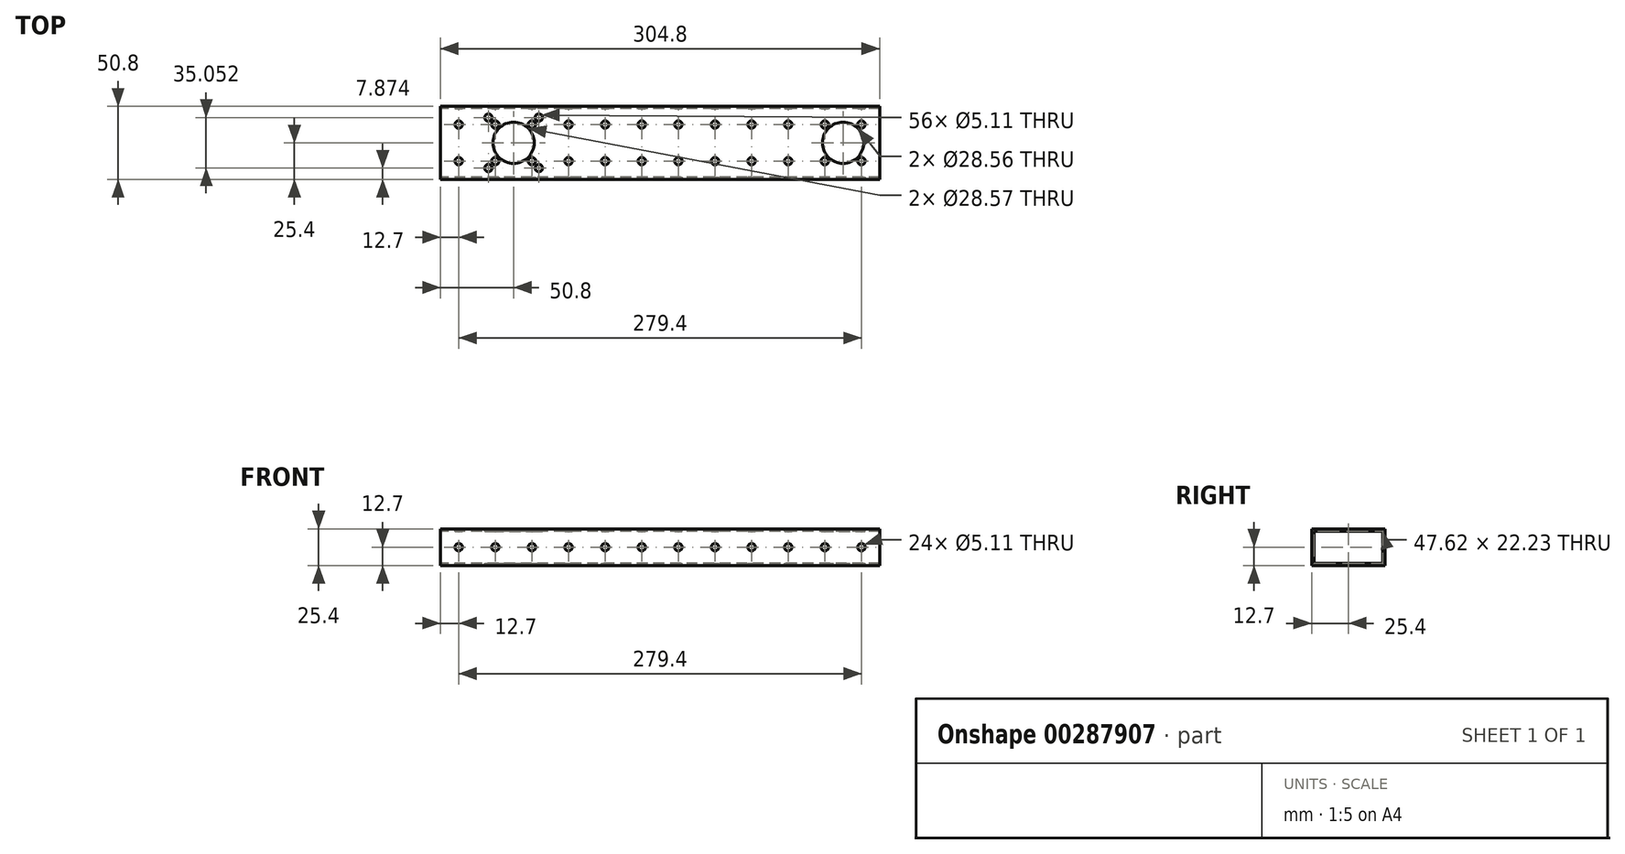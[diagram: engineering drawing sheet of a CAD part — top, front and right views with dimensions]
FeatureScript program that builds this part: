
annotation { "Feature Type Name" : "Feature", "Feature Type Description" : "" }
export const myFeature = defineFeature(function(context is Context, id is Id, definition is map)
    precondition{}
    {
        {
            var Q0;
            Q0=qCreatedBy(makeId("Right.planeOp"),FACE);
            var sketch = newSketch(context, id + "F0", { "sketchPlane" : qUnion([Q0])});
            skLineSegment(sketch, "E0.bottom", {"start": v(25.4, 12.7) * mm, "end": v(-25.4, 12.7) * mm});
            skLineSegment(sketch, "E0.top", {"start": v(25.4, -12.7) * mm, "end": v(-25.4, -12.7) * mm});
            skLineSegment(sketch, "E0.left", {"start": v(25.4, 12.7) * mm, "end": v(25.4, -12.7) * mm});
            skLineSegment(sketch, "E0.right", {"start": v(-25.4, 12.7) * mm, "end": v(-25.4, -12.7) * mm});
            skPoint(sketch, "E0.middle", {"position": v(0, 0) * mm});
            skLineSegment(sketch, "E1.bottom", {"start": v(23.81, 11.11) * mm, "end": v(-23.81, 11.11) * mm});
            skLineSegment(sketch, "E1.top", {"start": v(23.81, -11.11) * mm, "end": v(-23.81, -11.11) * mm});
            skLineSegment(sketch, "E1.left", {"start": v(23.81, 11.11) * mm, "end": v(23.81, -11.11) * mm});
            skLineSegment(sketch, "E1.right", {"start": v(-23.81, 11.11) * mm, "end": v(-23.81, -11.11) * mm});
            skSolve(sketch);
        }
        {
            var Q0;
            Q0 = qSketchRegion(id + "F0", true);
            extrude(context, id + "F1", {"entities" : qUnion([Q0]), "depth" : 304.8 * mm});
        }
        {
            var Q0;
            Q0=makeQuery(id+"F1.opExtrude","SWEPT_FACE",FACE,{"disambiguationData":[OSD([sQuery(id+"F0.wireOp",EDGE,"E0.bottom")])]});
            var sketch = newSketch(context, id + "F2", { "sketchPlane" : qUnion([Q0])});
            skCircle(sketch, "E2", {"center": v(279.4, 0) * mm, "radius": 14.28 * mm});
            skSolve(sketch);
        }
        {
            var Q0;
            Q0 = qSketchRegion(id + "F2", true);
            extrude(context, id + "F3", {"entities" : qUnion([Q0]), "operationType" : NewBodyOperationType.REMOVE, "endBound" : BoundingType.THROUGH_ALL, "oppositeDirection" : true, "depth" : 25.4 * mm});
        }
        {
            var Q0;
            Q0=makeQuery(id+"F1.opExtrude","SWEPT_FACE",FACE,{"disambiguationData":[OSD([sQuery(id+"F0.wireOp",EDGE,"E0.bottom")])]});
            var sketch = newSketch(context, id + "F4", { "sketchPlane" : qUnion([Q0])});
            skLineSegment(sketch, "E3", {"start": v(25.4, 25.4) * mm, "end": v(25.4, -25.4) * mm, "construction": true});
            skCircle(sketch, "E4", {"center": v(50.8, 0) * mm, "radius": 14.29 * mm});
            skLineSegment(sketch, "E5.bottom", {"start": v(68.33, -17.53) * mm, "end": v(33.27, -17.53) * mm, "construction": true});
            skLineSegment(sketch, "E5.top", {"start": v(68.33, 17.53) * mm, "end": v(33.27, 17.53) * mm, "construction": true});
            skLineSegment(sketch, "E5.left", {"start": v(68.33, -17.53) * mm, "end": v(68.33, 17.53) * mm, "construction": true});
            skLineSegment(sketch, "E5.right", {"start": v(33.27, -17.53) * mm, "end": v(33.27, 17.53) * mm, "construction": true});
            skCircle(sketch, "E6", {"center": v(68.33, 17.53) * mm, "radius": 2.55 * mm});
            skCircle(sketch, "E7", {"center": v(68.33, -17.53) * mm, "radius": 2.55 * mm});
            skCircle(sketch, "E8", {"center": v(33.27, -17.53) * mm, "radius": 2.55 * mm});
            skCircle(sketch, "E9", {"center": v(33.27, 17.53) * mm, "radius": 2.55 * mm});
            skPoint(sketch, "E10", {"position": v(279.4, 0) * mm});
            skSolve(sketch);
        }
        {
            var Q0;
            Q0 = qSketchRegion(id + "F4", true);
            extrude(context, id + "F5", {"entities" : qUnion([Q0]), "operationType" : NewBodyOperationType.REMOVE, "endBound" : BoundingType.THROUGH_ALL, "oppositeDirection" : true, "depth" : 25.4 * mm});
        }
        {
            var Q0;
            Q0=makeQuery(id+"F1.opExtrude","SWEPT_FACE",FACE,{"disambiguationData":[OSD([sQuery(id+"F0.wireOp",EDGE,"E0.right")])]});
            var sketch = newSketch(context, id + "F6", { "sketchPlane" : qUnion([Q0])});
            skCircle(sketch, "E11", {"center": v(12.7, 0) * mm, "radius": 2.55 * mm});
            skCircle(sketch, "E12.1.0.0", {"center": v(38.1, 0) * mm, "radius": 2.55 * mm});
            skCircle(sketch, "E12.2.0.0", {"center": v(63.5, 0) * mm, "radius": 2.55 * mm});
            skCircle(sketch, "E12.3.0.0", {"center": v(88.9, 0) * mm, "radius": 2.55 * mm});
            skCircle(sketch, "E12.4.0.0", {"center": v(114.3, 0) * mm, "radius": 2.55 * mm});
            skCircle(sketch, "E12.5.0.0", {"center": v(139.7, 0) * mm, "radius": 2.55 * mm});
            skCircle(sketch, "E12.6.0.0", {"center": v(165.1, 0) * mm, "radius": 2.55 * mm});
            skCircle(sketch, "E12.7.0.0", {"center": v(190.5, 0) * mm, "radius": 2.55 * mm});
            skCircle(sketch, "E12.8.0.0", {"center": v(215.9, 0) * mm, "radius": 2.55 * mm});
            skCircle(sketch, "E12.9.0.0", {"center": v(241.3, 0) * mm, "radius": 2.55 * mm});
            skCircle(sketch, "E12.10.0.0", {"center": v(266.7, 0) * mm, "radius": 2.55 * mm});
            skCircle(sketch, "E12.11.0.0", {"center": v(292.1, 0) * mm, "radius": 2.55 * mm});
            skLineSegment(sketch, "E12.direction1", {"start": v(12.7, 0) * mm, "end": v(38.1, 0) * mm, "construction": true});
            skSolve(sketch);
        }
        {
            var Q0;
            Q0=sQuery(id+"F6.wireOp",VERTEX,"E12.6.0.0.center");
            var Q1;
            Q1=sQuery(id+"F6.wireOp",VERTEX,"E12.5.0.0.center");
            var Q2;
            Q2=sQuery(id+"F6.wireOp",VERTEX,"E12.2.0.0.center");
            var Q3;
            Q3=sQuery(id+"F6.wireOp",VERTEX,"E12.4.0.0.center");
            var Q4;
            Q4=sQuery(id+"F6.wireOp",VERTEX,"E12.10.0.0.center");
            var Q5;
            Q5=sQuery(id+"F6.wireOp",VERTEX,"E12.3.0.0.center");
            var Q6;
            Q6=sQuery(id+"F6.wireOp",VERTEX,"E11.center");
            var Q7;
            Q7=sQuery(id+"F6.wireOp",VERTEX,"E12.7.0.0.center");
            var Q8;
            Q8=sQuery(id+"F6.wireOp",VERTEX,"E12.9.0.0.center");
            var Q9;
            Q9=sQuery(id+"F6.wireOp",VERTEX,"E12.8.0.0.center");
            var Q10;
            Q10=sQuery(id+"F6.wireOp",VERTEX,"E12.11.0.0.center");
            var Q11;
            Q11=sQuery(id+"F6.wireOp",VERTEX,"E12.direction1.end");
            var Q12;
            Q12=makeQuery(id+"F1.opExtrude","SWEPT_BODY",BODY,{"disambiguationData":[OSD([sQuery(id+"F0.wireOp",EDGE,"E0.bottom"),sQuery(id+"F0.wireOp",EDGE,"E0.top"),sQuery(id+"F0.wireOp",EDGE,"E0.left"),sQuery(id+"F0.wireOp",EDGE,"E0.right"),sQuery(id+"F0.wireOp",EDGE,"E1.bottom"),sQuery(id+"F0.wireOp",EDGE,"E1.top"),sQuery(id+"F0.wireOp",EDGE,"E1.left"),sQuery(id+"F0.wireOp",EDGE,"E1.right")])]});
            hole(context, id + "F7", {"style" : HoleStyle.SIMPLE, "endStyle" : HoleEndStyle.THROUGH, "holeDiameter" : 5.1 * mm, "tappedDepth" : 12.7 * mm, "tapClearance" : 3, "locations" : qUnion([Q0, Q1, Q2, Q3, Q4, Q5, Q6, Q7, Q8, Q9, Q10, Q11]), "scope" : qUnion([Q12])});
        }
        {
            var Q0;
            Q0=makeQuery(id+"F1.opExtrude","SWEPT_FACE",FACE,{"disambiguationData":[OSD([sQuery(id+"F0.wireOp",EDGE,"E0.bottom")])]});
            var sketch = newSketch(context, id + "F8", { "sketchPlane" : qUnion([Q0])});
            skCircle(sketch, "E13", {"center": v(12.7, 12.7) * mm, "radius": 2.55 * mm});
            skCircle(sketch, "E14.0.1.0", {"center": v(12.7, -12.7) * mm, "radius": 2.55 * mm});
            skCircle(sketch, "E14.1.0.0", {"center": v(38.1, 12.7) * mm, "radius": 2.55 * mm, "construction": true});
            skCircle(sketch, "E14.1.1.0", {"center": v(38.1, -12.7) * mm, "radius": 2.55 * mm, "construction": true});
            skCircle(sketch, "E14.2.0.0", {"center": v(63.5, 12.7) * mm, "radius": 2.55 * mm, "construction": true});
            skCircle(sketch, "E14.2.1.0", {"center": v(63.5, -12.7) * mm, "radius": 2.55 * mm, "construction": true});
            skCircle(sketch, "E14.3.0.0", {"center": v(88.9, 12.7) * mm, "radius": 2.55 * mm});
            skCircle(sketch, "E14.3.1.0", {"center": v(88.9, -12.7) * mm, "radius": 2.55 * mm});
            skCircle(sketch, "E14.4.0.0", {"center": v(114.3, 12.7) * mm, "radius": 2.55 * mm});
            skCircle(sketch, "E14.4.1.0", {"center": v(114.3, -12.7) * mm, "radius": 2.55 * mm});
            skCircle(sketch, "E14.5.0.0", {"center": v(139.7, 12.7) * mm, "radius": 2.55 * mm});
            skCircle(sketch, "E14.5.1.0", {"center": v(139.7, -12.7) * mm, "radius": 2.55 * mm});
            skCircle(sketch, "E14.6.0.0", {"center": v(165.1, 12.7) * mm, "radius": 2.55 * mm});
            skCircle(sketch, "E14.6.1.0", {"center": v(165.1, -12.7) * mm, "radius": 2.55 * mm});
            skCircle(sketch, "E14.7.0.0", {"center": v(190.5, 12.7) * mm, "radius": 2.55 * mm});
            skCircle(sketch, "E14.7.1.0", {"center": v(190.5, -12.7) * mm, "radius": 2.55 * mm});
            skCircle(sketch, "E14.8.0.0", {"center": v(215.9, 12.7) * mm, "radius": 2.55 * mm});
            skCircle(sketch, "E14.8.1.0", {"center": v(215.9, -12.7) * mm, "radius": 2.55 * mm});
            skCircle(sketch, "E14.9.0.0", {"center": v(241.3, 12.7) * mm, "radius": 2.55 * mm});
            skCircle(sketch, "E14.9.1.0", {"center": v(241.3, -12.7) * mm, "radius": 2.55 * mm});
            skCircle(sketch, "E14.10.0.0", {"center": v(266.7, 12.7) * mm, "radius": 2.55 * mm, "construction": true});
            skCircle(sketch, "E14.10.1.0", {"center": v(266.7, -12.7) * mm, "radius": 2.55 * mm, "construction": true});
            skCircle(sketch, "E14.11.0.0", {"center": v(292.1, 12.7) * mm, "radius": 2.55 * mm, "construction": true});
            skCircle(sketch, "E14.11.1.0", {"center": v(292.1, -12.7) * mm, "radius": 2.55 * mm, "construction": true});
            skLineSegment(sketch, "E14.direction1", {"start": v(12.7, 12.7) * mm, "end": v(38.1, 12.7) * mm, "construction": true});
            skLineSegment(sketch, "E14.direction2", {"start": v(12.7, 12.7) * mm, "end": v(12.7, -12.7) * mm, "construction": true});
            skSolve(sketch);
        }
        {
            var Q0;
            Q0=sQuery(id+"F8.wireOp",VERTEX,"E14.3.0.0.center");
            var Q1;
            Q1=sQuery(id+"F8.wireOp",VERTEX,"E14.6.1.0.center");
            var Q2;
            Q2=sQuery(id+"F8.wireOp",VERTEX,"E14.9.1.0.center");
            var Q3;
            Q3=sQuery(id+"F8.wireOp",VERTEX,"E14.5.1.0.center");
            var Q4;
            Q4=sQuery(id+"F8.wireOp",VERTEX,"E14.1.0.0.center");
            var Q5;
            Q5=sQuery(id+"F8.wireOp",VERTEX,"E14.6.0.0.center");
            var Q6;
            Q6=sQuery(id+"F8.wireOp",VERTEX,"E14.8.1.0.center");
            var Q7;
            Q7=sQuery(id+"F8.wireOp",VERTEX,"E14.11.0.0.center");
            var Q8;
            Q8=sQuery(id+"F8.wireOp",VERTEX,"E14.10.1.0.center");
            var Q9;
            Q9=sQuery(id+"F8.wireOp",VERTEX,"E14.2.1.0.center");
            var Q10;
            Q10=sQuery(id+"F8.wireOp",VERTEX,"E14.3.1.0.center");
            var Q11;
            Q11=sQuery(id+"F8.wireOp",VERTEX,"E14.10.0.0.center");
            var Q12;
            Q12=sQuery(id+"F8.wireOp",VERTEX,"E14.9.0.0.center");
            var Q13;
            Q13=sQuery(id+"F8.wireOp",VERTEX,"E14.2.0.0.center");
            var Q14;
            Q14=sQuery(id+"F8.wireOp",VERTEX,"E14.1.1.0.center");
            var Q15;
            Q15=sQuery(id+"F8.wireOp",VERTEX,"E14.7.0.0.center");
            var Q16;
            Q16=sQuery(id+"F8.wireOp",VERTEX,"E14.direction1.start");
            var Q17;
            Q17=sQuery(id+"F8.wireOp",VERTEX,"E14.0.1.0.center");
            var Q18;
            Q18=sQuery(id+"F8.wireOp",VERTEX,"E14.4.1.0.center");
            var Q19;
            Q19=sQuery(id+"F8.wireOp",VERTEX,"E14.4.0.0.center");
            var Q20;
            Q20=sQuery(id+"F8.wireOp",VERTEX,"E14.11.1.0.center");
            var Q21;
            Q21=sQuery(id+"F8.wireOp",VERTEX,"E14.5.0.0.center");
            var Q22;
            Q22=sQuery(id+"F8.wireOp",VERTEX,"E14.7.1.0.center");
            var Q23;
            Q23=sQuery(id+"F8.wireOp",VERTEX,"E14.8.0.0.center");
            var Q24;
            Q24=makeQuery(id+"F1.opExtrude","SWEPT_BODY",BODY,{"disambiguationData":[OSD([sQuery(id+"F0.wireOp",EDGE,"E0.bottom"),sQuery(id+"F0.wireOp",EDGE,"E0.top"),sQuery(id+"F0.wireOp",EDGE,"E0.left"),sQuery(id+"F0.wireOp",EDGE,"E0.right"),sQuery(id+"F0.wireOp",EDGE,"E1.bottom"),sQuery(id+"F0.wireOp",EDGE,"E1.top"),sQuery(id+"F0.wireOp",EDGE,"E1.left"),sQuery(id+"F0.wireOp",EDGE,"E1.right")])]});
            hole(context, id + "F9", {"style" : HoleStyle.SIMPLE, "endStyle" : HoleEndStyle.THROUGH, "holeDiameter" : 5.1 * mm, "tappedDepth" : 12.7 * mm, "tapClearance" : 3, "locations" : qUnion([Q0, Q1, Q2, Q3, Q4, Q5, Q6, Q7, Q8, Q9, Q10, Q11, Q12, Q13, Q14, Q15, Q16, Q17, Q18, Q19, Q20, Q21, Q22, Q23]), "scope" : qUnion([Q24])});
        }
    });
